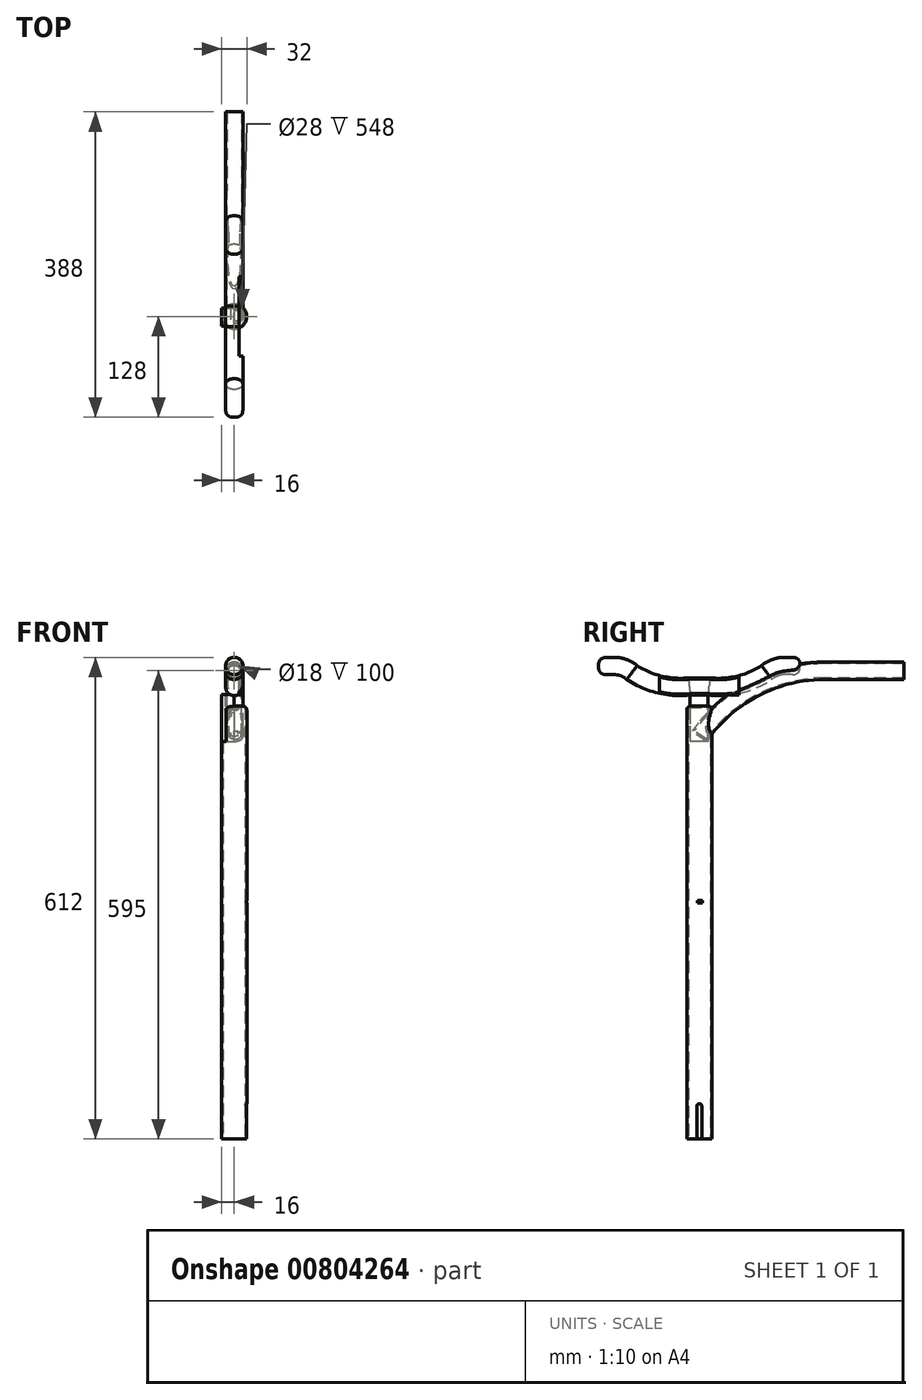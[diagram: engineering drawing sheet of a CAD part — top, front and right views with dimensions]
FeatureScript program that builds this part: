
annotation { "Feature Type Name" : "Feature", "Feature Type Description" : "" }
export const myFeature = defineFeature(function(context is Context, id is Id, definition is map)
    precondition{}
    {
        {
            var Q0;
            Q0=qCreatedBy(makeId("Top.planeOp"),FACE);
            var sketch = newSketch(context, id + "F0", { "sketchPlane" : qUnion([Q0])});
            skCircle(sketch, "E0", {"center": v(0, 0) * mm, "radius": 16 * mm});
            skSolve(sketch);
        }
        {
            var Q0;
            Q0 = qSketchRegion(id + "F0", true);
            extrude(context, id + "F1", {"entities" : qUnion([Q0]), "depth" : 550 * mm, "offsetDistance" : 25 * mm});
        }
        {
            var Q0;
            Q0=makeQuery(id+"F1.opExtrude","CAP_FACE",FACE,{"disambiguationData":[OSD([sQuery(id+"F0.wireOp",EDGE,"E0")])],"isStart":true});
            shell(context, id + "F2", {"entities" : qUnion([Q0]), "thickness" : 2 * mm});
        }
        {
            var Q0;
            Q0=qCreatedBy(makeId("Right.planeOp"),FACE);
            var sketch = newSketch(context, id + "F3", { "sketchPlane" : qUnion([Q0])});
            skLineSegment(sketch, "E1.bottom", {"start": v(3, 0) * mm, "end": v(-3, 0) * mm});
            skLineSegment(sketch, "E1.top", {"start": v(0, 45) * mm, "end": v(0, 45) * mm});
            skLineSegment(sketch, "E1.left", {"start": v(3, 0) * mm, "end": v(3, 42) * mm});
            skLineSegment(sketch, "E1.right", {"start": v(-3, 0) * mm, "end": v(-3, 42) * mm});
            skPoint(sketch, "E2.visualSharp", {"position": v(-3, 45) * mm});
            skArc(sketch, "E2.filletArc", {"start": v(0, 45) * mm, "mid": v(-2.12, 44.12) * mm, "end": v(-3, 42) * mm});
            skPoint(sketch, "E3.visualSharp", {"position": v(3, 45) * mm});
            skArc(sketch, "E3.filletArc", {"start": v(3, 42) * mm, "mid": v(2.12, 44.12) * mm, "end": v(0, 45) * mm});
            skSolve(sketch);
        }
        {
            var Q0;
            Q0 = qSketchRegion(id + "F3", true);
            extrude(context, id + "F4", {"entities" : qUnion([Q0]), "operationType" : NewBodyOperationType.REMOVE, "endBound" : BoundingType.THROUGH_ALL, "depth" : 25 * mm, "offsetDistance" : 25 * mm});
        }
        {
            var Q0;
            Q0=qCreatedBy(makeId("Right.planeOp"),FACE);
            var sketch = newSketch(context, id + "F5", { "sketchPlane" : qUnion([Q0])});
            skArc(sketch, "E4", {"start": v(160, 595) * mm, "mid": v(69.75, 572.86) * mm, "end": v(0, 511.47) * mm});
            skLineSegment(sketch, "E5", {"start": v(160, 595) * mm, "end": v(260, 595) * mm});
            skSolve(sketch);
        }
        {
            var Q0;
            Q0=sQuery(id+"F5.wireOp",VERTEX,"E5.end");
            var Q1;
            Q1=qCreatedBy(makeId("Front.planeOp"),FACE);
            cPlane(context, id + "F6", {"entities" : qUnion([Q0, Q1]), "cplaneType" : CPlaneType.PLANE_POINT, "offset" : 25 * mm, "width" : 150 * mm, "height" : 150 * mm});
        }
        {
            var Q0;
            Q0=qCreatedBy(id+"F6.planeOp",FACE);
            var sketch = newSketch(context, id + "F7", { "sketchPlane" : qUnion([Q0])});
            skCircle(sketch, "E6", {"center": v(0, 595) * mm, "radius": 11 * mm});
            skSolve(sketch);
        }
        {
            var Q0;
            Q0 = qSketchRegion(id + "F7", true);
            var Q1;
            Q1 = qConstructionFilter(qBodyType(qCreatedBy(id + "F5" ,EDGE), BodyType.WIRE), ConstructionObject.NO);
            sweep(context, id + "F8", {"operationType" : NewBodyOperationType.ADD, "profiles" : qUnion([Q0]), "path" : qUnion([Q1])});
        }
        {
            var Q0;
            Q0=makeQuery(id+"F8.opSweep","CAP_FACE",FACE,{"disambiguationData":[OSD([sQuery(id+"F5.wireOp",VERTEX,"E5.end"),sQuery(id+"F7.wireOp",EDGE,"E6")])],"isStart":true});
            shell(context, id + "F9", {"entities" : qUnion([Q0]), "thickness" : 2 * mm});
        }
        {
            var Q0;
            Q0=qCreatedBy(makeId("Right.planeOp"),FACE);
            var sketch = newSketch(context, id + "F10", { "sketchPlane" : qUnion([Q0])});
            skLineSegment(sketch, "E7", {"start": v(0, 531.74) * mm, "end": v(0, 575) * mm, "construction": true});
            skLineSegment(sketch, "E8", {"start": v(-128, 601) * mm, "end": v(-108, 601) * mm});
            skArc(sketch, "E9", {"start": v(-85.62, 592.66) * mm, "mid": v(-96.06, 598.85) * mm, "end": v(-108, 601) * mm});
            skArc(sketch, "E10", {"start": v(-85.62, 592.66) * mm, "mid": v(-50.59, 577.5) * mm, "end": v(-12.5, 575) * mm});
            skLineSegment(sketch, "E11", {"start": v(-12.5, 575) * mm, "end": v(0, 575) * mm});
            skLineSegment(sketch, "E12.MirrorCS", {"start": v(12.5, 575) * mm, "end": v(0, 575) * mm});
            skArc(sketch, "E13.MirrorCS", {"start": v(85.62, 592.66) * mm, "mid": v(50.59, 577.5) * mm, "end": v(12.5, 575) * mm});
            skArc(sketch, "E14.MirrorCS", {"start": v(85.62, 592.66) * mm, "mid": v(96.06, 598.85) * mm, "end": v(108, 601) * mm});
            skLineSegment(sketch, "E15.MirrorCS", {"start": v(128, 601) * mm, "end": v(108, 601) * mm});
            skSolve(sketch);
        }
        {
            var Q0;
            Q0=sQuery(id+"F10.wireOp",VERTEX,"E15.MirrorCS.start");
            var Q1;
            Q1=qCreatedBy(id+"F6.planeOp",FACE);
            cPlane(context, id + "F11", {"entities" : qUnion([Q0, Q1]), "cplaneType" : CPlaneType.PLANE_POINT, "offset" : 25 * mm, "width" : 150 * mm, "height" : 150 * mm});
        }
        {
            var Q0;
            Q0=qCreatedBy(id+"F11.planeOp",FACE);
            var sketch = newSketch(context, id + "F12", { "sketchPlane" : qUnion([Q0])});
            skCircle(sketch, "E16", {"center": v(0, 601) * mm, "radius": 11 * mm});
            skSolve(sketch);
        }
        {
            var Q0;
            Q0 = qSketchRegion(id + "F12", true);
            var Q1;
            Q1 = qConstructionFilter(qBodyType(qCreatedBy(id + "F10" ,EDGE), BodyType.WIRE), ConstructionObject.NO);
            sweep(context, id + "F13", {"profiles" : qUnion([Q0]), "path" : qUnion([Q1])});
        }
        {
            var Q0;
            Q0=makeQuery(id+"F13.opSweep","CAP_EDGE",EDGE,{"disambiguationData":[OSD([sQuery(id+"F10.wireOp",VERTEX,"E15.MirrorCS.start"),sQuery(id+"F12.wireOp",EDGE,"E16")])],"isStart":true});
            var Q1;
            Q1=makeQuery(id+"F13.opSweep","CAP_EDGE",EDGE,{"disambiguationData":[OSD([sQuery(id+"F10.wireOp",VERTEX,"E8.start"),sQuery(id+"F12.wireOp",EDGE,"E16")])],"isStart":false});
            fillet(context, id + "F14", {"entities" : qUnion([Q0, Q1]), "radius" : 10 * mm, "tangentPropagation" : true, "rho" : 0.5, "crossSection" : FilletCrossSection.CONIC, "allowEdgeOverflow" : false});
        }
        {
            var Q0;
            Q0=makeQuery(id+"F1.opExtrude","CAP_EDGE",EDGE,{"disambiguationData":[OSD([sQuery(id+"F0.wireOp",EDGE,"E0")])],"isStart":false});
            fillet(context, id + "F15", {"entities" : qUnion([Q0]), "radius" : 5 * mm, "tangentPropagation" : true, "allowEdgeOverflow" : false});
        }
        {
            var Q0;
            Q0=qCreatedBy(makeId("Right.planeOp"),FACE);
            var sketch = newSketch(context, id + "F16", { "sketchPlane" : qUnion([Q0])});
            skArc(sketch, "E17.cCircle", {"start": v(-56.39, 589.3) * mm, "mid": v(0, 489.4) * mm, "end": v(56.39, 589.3) * mm, "construction": true});
            skLineSegment(sketch, "E17.0", {"start": v(56.39, 589.3) * mm, "end": v(76.04, 556.74) * mm});
            skLineSegment(sketch, "E17.1", {"start": v(76.04, 556.74) * mm, "end": v(39.3, 490.15) * mm});
            skLineSegment(sketch, "E17.2", {"start": v(39.3, 490.15) * mm, "end": v(-36.73, 488.67) * mm});
            skLineSegment(sketch, "E17.3", {"start": v(-36.73, 488.67) * mm, "end": v(-76.04, 553.77) * mm});
            skLineSegment(sketch, "E17.4", {"start": v(-76.04, 553.77) * mm, "end": v(-56.44, 589.3) * mm});
            skPoint(sketch, "E17.0.midPoint", {"position": v(56.39, 589.3) * mm});
            skLineSegment(sketch, "E18", {"start": v(56.39, 589.3) * mm, "end": v(-56.44, 589.3) * mm});
            skPoint(sketch, "E17.5.end.orphan", {"position": v(36.73, 621.85) * mm});
            skPoint(sketch, "E19.orphan", {"position": v(-39.3, 620.37) * mm});
            skSolve(sketch);
        }
        {
            var Q0;
            Q0 = qSketchRegion(id + "F16", true);
            extrude(context, id + "F17", {"entities" : qUnion([Q0]), "depth" : 90 * mm, "offsetDistance" : 25 * mm});
        }
        {
            var Q0;
            Q0=makeQuery(id+"F17.opExtrude","SWEPT_FACE",FACE,{"disambiguationData":[OSD([sQuery(id+"F16.wireOp",EDGE,"E18")])]});
            var Q1;
            Q1=makeQuery(id+"F17.opExtrude","SWEPT_BODY",BODY,{"disambiguationData":[OSD([sQuery(id+"F16.wireOp",EDGE,"E17.0"),sQuery(id+"F16.wireOp",EDGE,"E17.1"),sQuery(id+"F16.wireOp",EDGE,"E17.2"),sQuery(id+"F16.wireOp",EDGE,"E17.3"),sQuery(id+"F16.wireOp",EDGE,"E17.4"),sQuery(id+"F16.wireOp",EDGE,"E18")])]});
            shell(context, id + "F18", {"isHollow" : true, "entities" : qUnion([Q0]), "parts" : qUnion([Q1]), "thickness" : 6 * mm});
        }
        {
            var Q0;
            Q0=makeQuery(id+"F17.opExtrude","SWEPT_FACE",FACE,{"disambiguationData":[OSD([sQuery(id+"F16.wireOp",EDGE,"E18")])]});
            var sketch = newSketch(context, id + "F19", { "sketchPlane" : qUnion([Q0])});
            skSolve(sketch);
        }
        {
            var Q0;
            {var subQ0=sQuery(id+"F16.wireOp",EDGE,"E18");Q0=makeQuery(id+"F19.imprint","IMPRINT",FACE,{"disambiguationData":[TD([[makeQuery(id+"F19.imprint","IMPRINT",EDGE,{"derivedFrom":makeQuery(id+"F17.opExtrude","CAP_EDGE",EDGE,{"disambiguationData":[OSD([subQ0])],"isStart":true})}),1.0]])]});}
            var sketch = newSketch(context, id + "F20", { "sketchPlane" : qUnion([Q0])});
            skLineSegment(sketch, "E20.bottom", {"start": v(6, 50.39) * mm, "end": v(84, 50.39) * mm});
            skLineSegment(sketch, "E20.top", {"start": v(6, -50.44) * mm, "end": v(84, -50.44) * mm});
            skLineSegment(sketch, "E20.left", {"start": v(6, 50.39) * mm, "end": v(6, -50.44) * mm});
            skLineSegment(sketch, "E20.right", {"start": v(84, 50.39) * mm, "end": v(84, -50.44) * mm});
            skPoint(sketch, "E20.middle", {"position": v(45, -0.03) * mm});
            skSolve(sketch);
        }
        {
            var Q0;
            Q0 = qSketchRegion(id + "F20", true);
            extrude(context, id + "F21", {"entities" : qUnion([Q0]), "operationType" : NewBodyOperationType.REMOVE, "oppositeDirection" : true, "depth" : 25 * mm, "offsetDistance" : 25 * mm});
        }
        {
            var Q0;
            Q0=makeQuery(id+"F17.opExtrude","SWEPT_BODY",BODY,{"disambiguationData":[OSD([sQuery(id+"F16.wireOp",EDGE,"E17.0"),sQuery(id+"F16.wireOp",EDGE,"E17.1"),sQuery(id+"F16.wireOp",EDGE,"E17.2"),sQuery(id+"F16.wireOp",EDGE,"E17.3"),sQuery(id+"F16.wireOp",EDGE,"E17.4"),sQuery(id+"F16.wireOp",EDGE,"E18")])]});
            transform(context, id + "F22", {"entities" : qUnion([Q0]), "transformType" : TransformType.TRANSLATION_3D, "dx" : 10 * mm, "dy" : 0 * mm, "dz" : 0 * mm, "makeCopy" : false});
        }
        {
            var Q0;
            Q0=makeQuery(id+"F17.opExtrude","SWEPT_BODY",BODY,{"disambiguationData":[OSD([sQuery(id+"F16.wireOp",EDGE,"E17.0"),sQuery(id+"F16.wireOp",EDGE,"E17.1"),sQuery(id+"F16.wireOp",EDGE,"E17.2"),sQuery(id+"F16.wireOp",EDGE,"E17.3"),sQuery(id+"F16.wireOp",EDGE,"E17.4"),sQuery(id+"F16.wireOp",EDGE,"E18")])]});
            deleteBodies(context, id + "F23", {"entities" : qUnion([Q0])});
        }
        {
            var Q0;
            Q0=qCreatedBy(makeId("Right.planeOp"),FACE);
            var sketch = newSketch(context, id + "F24", { "sketchPlane" : qUnion([Q0])});
            skLineSegment(sketch, "E21.bottom", {"start": v(-2.38, 303.27) * mm, "end": v(3.92, 303.27) * mm});
            skLineSegment(sketch, "E21.top", {"start": v(-2.38, 300) * mm, "end": v(3.92, 300) * mm});
            skLineSegment(sketch, "E21.left", {"start": v(-2.38, 303.27) * mm, "end": v(-2.38, 300) * mm});
            skLineSegment(sketch, "E21.right", {"start": v(3.92, 303.27) * mm, "end": v(3.92, 300) * mm});
            skSolve(sketch);
        }
        {
            var Q0;
            Q0 = qSketchRegion(id + "F24", true);
            extrude(context, id + "F25", {"entities" : qUnion([Q0]), "operationType" : NewBodyOperationType.REMOVE, "depth" : 25 * mm, "offsetDistance" : 25 * mm});
        }
        {
            var Q0;
            Q0=qCreatedBy(makeId("Right.planeOp"),FACE);
            var sketch = newSketch(context, id + "F26", { "sketchPlane" : qUnion([Q0])});
            skLineSegment(sketch, "E22.bottom", {"start": v(10.88, 565) * mm, "end": v(-12.12, 565) * mm});
            skLineSegment(sketch, "E22.top", {"start": v(10.88, 505) * mm, "end": v(-12.12, 505) * mm});
            skLineSegment(sketch, "E22.left", {"start": v(10.88, 565) * mm, "end": v(10.88, 505) * mm});
            skLineSegment(sketch, "E22.right", {"start": v(-12.12, 565) * mm, "end": v(-12.12, 505) * mm});
            skPoint(sketch, "E23", {"position": v(10.88, 524.54) * mm});
            skSolve(sketch);
        }
        {
            var Q0;
            Q0 = qSketchRegion(id + "F26", true);
            extrude(context, id + "F27", {"entities" : qUnion([Q0]), "operationType" : NewBodyOperationType.ADD, "oppositeDirection" : true, "depth" : 16 * mm, "offsetDistance" : 25 * mm});
        }
    });
